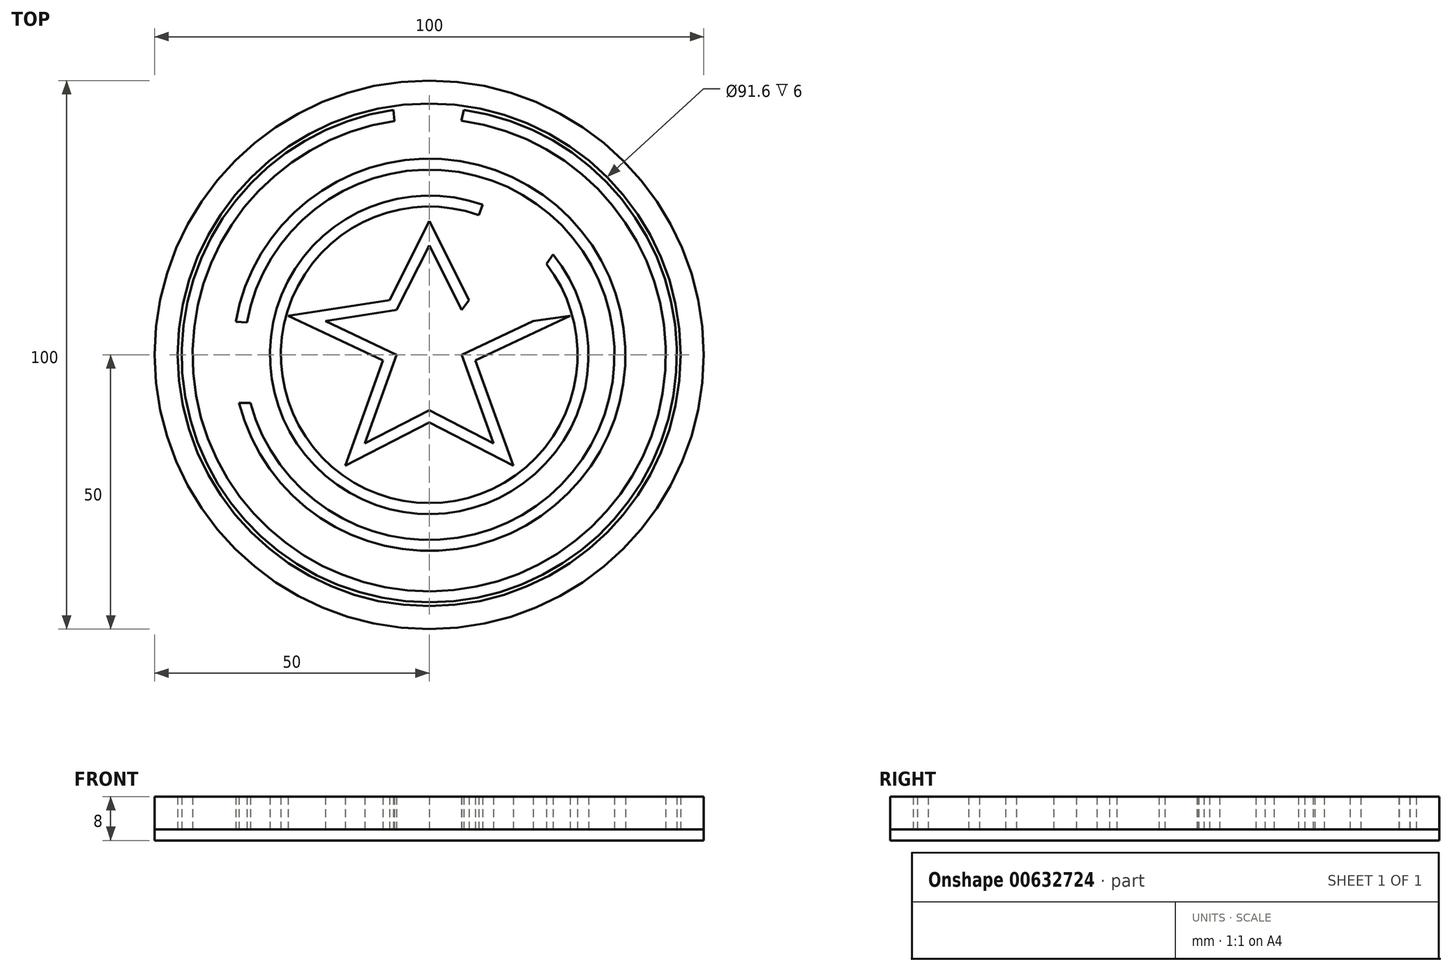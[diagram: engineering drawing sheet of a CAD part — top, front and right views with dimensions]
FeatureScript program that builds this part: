
annotation { "Feature Type Name" : "Feature", "Feature Type Description" : "" }
export const myFeature = defineFeature(function(context is Context, id is Id, definition is map)
    precondition{}
    {
        {
            var Q0;
            Q0=qCreatedBy(makeId("Top.planeOp"),FACE);
            var sketch = newSketch(context, id + "F0", { "sketchPlane" : qUnion([Q0])});
            skCircle(sketch, "E0", {"center": v(0, 0) * mm, "radius": 50 * mm});
            skLineSegment(sketch, "E1", {"start": v(0, 19.91) * mm, "end": v(-5.93, 8.16) * mm});
            skLineSegment(sketch, "E2", {"start": v(5.93, 8.16) * mm, "end": v(0, 19.91) * mm});
            skLineSegment(sketch, "E3", {"start": v(-5.93, 8.16) * mm, "end": v(-18.94, 6.15) * mm});
            skLineSegment(sketch, "E4", {"start": v(-18.94, 6.15) * mm, "end": v(-5.93, 0) * mm});
            skLineSegment(sketch, "E5", {"start": v(18.94, 6.15) * mm, "end": v(5.93, 0) * mm});
            skLineSegment(sketch, "E6", {"start": v(-5.93, 0) * mm, "end": v(-11.7, -16.1) * mm});
            skLineSegment(sketch, "E7", {"start": v(5.93, 0) * mm, "end": v(11.7, -16.1) * mm});
            skLineSegment(sketch, "E8", {"start": v(11.7, -16.1) * mm, "end": v(0, -10.08) * mm});
            skLineSegment(sketch, "E9", {"start": v(-11.7, -16.1) * mm, "end": v(0, -10.08) * mm});
            skLineSegment(sketch, "E10", {"start": v(18.59, 14.61) * mm, "end": v(18.59, 14.61) * mm});
            skLineSegment(sketch, "E11.0", {"start": v(7.25, 9.98) * mm, "end": v(0, 24.35) * mm});
            skLineSegment(sketch, "E11.2", {"start": v(0, 24.35) * mm, "end": v(-7.25, 9.98) * mm});
            skLineSegment(sketch, "E11.3", {"start": v(25.7, 7.14) * mm, "end": v(8.42, -1.03) * mm});
            skLineSegment(sketch, "E11.4", {"start": v(8.42, -1.03) * mm, "end": v(15.3, -20.2) * mm});
            skLineSegment(sketch, "E11.5", {"start": v(15.3, -20.2) * mm, "end": v(0, -12.33) * mm});
            skLineSegment(sketch, "E11.6", {"start": v(-7.25, 9.98) * mm, "end": v(-25.7, 7.14) * mm});
            skLineSegment(sketch, "E11.7", {"start": v(-25.7, 7.14) * mm, "end": v(-8.42, -1.03) * mm});
            skLineSegment(sketch, "E11.8", {"start": v(-8.42, -1.03) * mm, "end": v(-15.3, -20.2) * mm});
            skLineSegment(sketch, "E11.9", {"start": v(-15.3, -20.2) * mm, "end": v(0, -12.33) * mm});
            skArc(sketch, "E12", {"start": v(-6.52, 44.62) * mm, "mid": v(0.1, -45.1) * mm, "end": v(6.32, 44.65) * mm});
            skArc(sketch, "E13", {"start": v(-6.3, 42.63) * mm, "mid": v(0.24, -43.1) * mm, "end": v(5.83, 42.7) * mm});
            skArc(sketch, "E14", {"start": v(-34.65, -8.75) * mm, "mid": v(35.7, 1.4) * mm, "end": v(-35.23, 6) * mm});
            skArc(sketch, "E15", {"start": v(-32.58, -8.76) * mm, "mid": v(33.7, 1.47) * mm, "end": v(-33.22, 5.9) * mm});
            skArc(sketch, "E16", {"start": v(9.71, 27.35) * mm, "mid": v(-16.76, -23.7) * mm, "end": v(22.55, 18.27) * mm});
            skArc(sketch, "E17", {"start": v(9, 25.47) * mm, "mid": v(-15.8, -21.92) * mm, "end": v(21.32, 16.6) * mm});
            skLineSegment(sketch, "E18", {"start": v(18.94, 6.15) * mm, "end": v(25.7, 7.14) * mm});
            skLineSegment(sketch, "E19", {"start": v(5.93, 8.16) * mm, "end": v(7.25, 9.98) * mm});
            skLineSegment(sketch, "E20", {"start": v(-32.58, -8.76) * mm, "end": v(-34.65, -8.75) * mm});
            skLineSegment(sketch, "E21", {"start": v(-35.23, 6) * mm, "end": v(-33.22, 5.9) * mm});
            skLineSegment(sketch, "E22", {"start": v(9.71, 27.35) * mm, "end": v(9, 25.47) * mm});
            skLineSegment(sketch, "E23", {"start": v(22.55, 18.27) * mm, "end": v(21.32, 16.6) * mm});
            skLineSegment(sketch, "E24", {"start": v(5.83, 42.7) * mm, "end": v(6.32, 44.65) * mm});
            skLineSegment(sketch, "E25", {"start": v(-6.3, 42.63) * mm, "end": v(-6.52, 44.62) * mm});
            skCircle(sketch, "E26.0", {"center": v(0, 0) * mm, "radius": 45.8 * mm});
            skSolve(sketch);
        }
        {
            var Q0;
            Q0 = qSketchRegion(id + "F0", true);
            var Q1;
            Q1=makeQuery(id+"F0.imprint","IMPRINT",FACE,{"disambiguationData":[TD([[makeQuery(id+"F0.imprint","IMPRINT",EDGE,{"derivedFrom":sQuery(id+"F0.wireOp",EDGE,"52e8dcad-2c2c-4858-8885-f27ac76ef22b.0")}),1.0]])]});
            var Q2;
            Q2=makeQuery(id+"F0.imprint","IMPRINT",FACE,{"disambiguationData":[TD([[makeQuery(id+"F0.imprint","IMPRINT",EDGE,{"derivedFrom":sQuery(id+"F0.wireOp",EDGE,"8ab321e6-c0e5-4c45-b4aa-7db5fb8d522f.0")}),1.0]])]});
            var Q3;
            Q3=makeQuery(id+"F0.imprint","IMPRINT",FACE,{"disambiguationData":[TD([[makeQuery(id+"F0.imprint","IMPRINT",EDGE,{"derivedFrom":sQuery(id+"F0.wireOp",EDGE,"c3809c90-e4e6-46cd-a916-0e16c796eda5.0")}),1.0]])]});
            var Q4;
            Q4=makeQuery(id+"F0.imprint","IMPRINT",FACE,{"disambiguationData":[TD([[makeQuery(id+"F0.imprint","IMPRINT",EDGE,{"derivedFrom":sQuery(id+"F0.wireOp",EDGE,"E1")}),-1.0]])]});
            var Q5;
            Q5=makeQuery(id+"F0.imprint","IMPRINT",FACE,{"disambiguationData":[TD([[makeQuery(id+"F0.imprint","IMPRINT",EDGE,{"derivedFrom":sQuery(id+"F0.wireOp",EDGE,"yHiTNWfK-upAT-LlGf-Z4ck-qECjF3hW2dXV")}),1.0]])]});
            var Q6;
            Q6=makeQuery(id+"F0.imprint","IMPRINT",FACE,{"disambiguationData":[TD([[makeQuery(id+"F0.imprint","IMPRINT",EDGE,{"derivedFrom":sQuery(id+"F0.wireOp",EDGE,"JJYxRTPm-FJyn-789n-JMVY-6Vz2ZohTuZnW")}),1.0]])]});
            var Q7;
            Q7=makeQuery(id+"F0.imprint","IMPRINT",FACE,{"disambiguationData":[TD([[makeQuery(id+"F0.imprint","IMPRINT",EDGE,{"derivedFrom":sQuery(id+"F0.wireOp",EDGE,"Yx9YfQBW-IfdX-yKP6-UOXm-zSYYP024VBGi")}),1.0]])]});
            var Q8;
            Q8=makeQuery(id+"F0.imprint","IMPRINT",FACE,{"disambiguationData":[TD([[makeQuery(id+"F0.imprint","IMPRINT",EDGE,{"derivedFrom":sQuery(id+"F0.wireOp",EDGE,"80xAxvJt-7wRB-bVA9-flTW-FWlteCIhMRqz")}),-1.0]])]});
            var Q9;
            Q9=makeQuery(id+"F0.imprint","IMPRINT",FACE,{"disambiguationData":[TD([[makeQuery(id+"F0.imprint","IMPRINT",EDGE,{"derivedFrom":sQuery(id+"F0.wireOp",EDGE,"E1")}),1.0]])]});
            var Q10;
            Q10=makeQuery(id+"F0.imprint","IMPRINT",FACE,{"disambiguationData":[TD([[makeQuery(id+"F0.imprint","IMPRINT",EDGE,{"derivedFrom":sQuery(id+"F0.wireOp",EDGE,"E12")}),1.0]])]});
            var Q11;
            Q11=makeQuery(id+"F0.imprint","IMPRINT",FACE,{"disambiguationData":[TD([[makeQuery(id+"F0.imprint","IMPRINT",EDGE,{"derivedFrom":sQuery(id+"F0.wireOp",EDGE,"E14")}),1.0]])]});
            var Q12;
            Q12=makeQuery(id+"F0.imprint","IMPRINT",FACE,{"disambiguationData":[TD([[makeQuery(id+"F0.imprint","IMPRINT",EDGE,{"derivedFrom":sQuery(id+"F0.wireOp",EDGE,"E16")}),1.0]])]});
            extrude(context, id + "F1", {"entities" : qUnion([Q0, Q1, Q2, Q3, Q4, Q5, Q6, Q7, Q8, Q9, Q10, Q11, Q12]), "oppositeDirection" : true, "depth" : 2 * mm, "offsetDistance" : 25 * mm});
        }
        {
            var Q0;
            Q0=makeQuery(id+"F0.imprint","IMPRINT",FACE,{"disambiguationData":[TD([[makeQuery(id+"F0.imprint","IMPRINT",EDGE,{"derivedFrom":sQuery(id+"F0.wireOp",EDGE,"E12")}),1.0]])]});
            var Q1;
            Q1=makeQuery(id+"F0.imprint","IMPRINT",FACE,{"disambiguationData":[TD([[makeQuery(id+"F0.imprint","IMPRINT",EDGE,{"derivedFrom":sQuery(id+"F0.wireOp",EDGE,"E16")}),1.0]])]});
            var Q2;
            Q2=makeQuery(id+"F0.imprint","IMPRINT",FACE,{"disambiguationData":[TD([[makeQuery(id+"F0.imprint","IMPRINT",EDGE,{"derivedFrom":sQuery(id+"F0.wireOp",EDGE,"E14")}),1.0]])]});
            var Q3;
            Q3=makeQuery(id+"F0.imprint","IMPRINT",FACE,{"disambiguationData":[TD([[makeQuery(id+"F0.imprint","IMPRINT",EDGE,{"derivedFrom":sQuery(id+"F0.wireOp",EDGE,"E1")}),-1.0]])]});
            extrude(context, id + "F2", {"entities" : qUnion([Q0, Q1, Q2, Q3]), "operationType" : NewBodyOperationType.ADD, "depth" : 6 * mm, "offsetDistance" : 25 * mm});
        }
        {
            var Q0;
            Q0=makeQuery(id+"F0.imprint","IMPRINT",FACE,{"disambiguationData":[TD([[makeQuery(id+"F0.imprint","IMPRINT",EDGE,{"derivedFrom":sQuery(id+"F0.wireOp",EDGE,"E0")}),1.0]])]});
            extrude(context, id + "F3", {"entities" : qUnion([Q0]), "depth" : 6 * mm, "offsetDistance" : 25 * mm});
        }
    });
